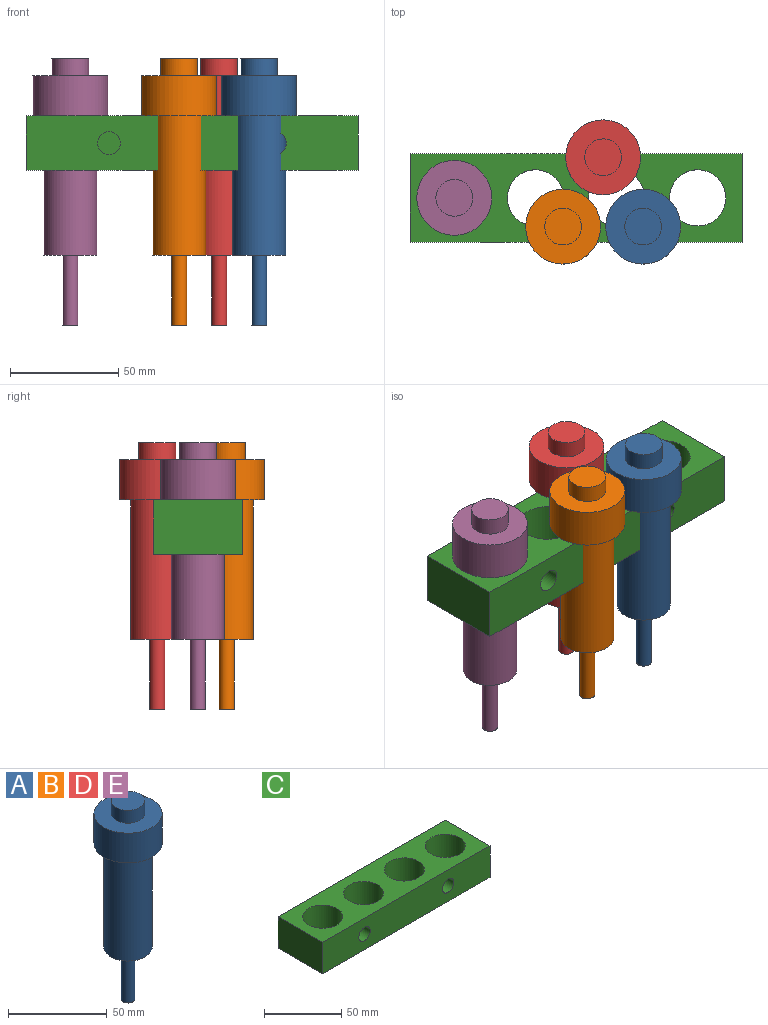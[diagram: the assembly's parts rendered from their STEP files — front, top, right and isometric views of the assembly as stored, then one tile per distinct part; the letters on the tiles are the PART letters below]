
ASSEMBLY  parts=5 mates=1
PART A: 9 faces, bbox 34.6x34.6x123.3 mm
  f0: plane 34.6x34.6mm, normal (0,0,1), area 713.3mm2, adj f1,f7
  f1: cylinder r=17.3mm len=34.6mm, axis (0,0,1), area 2010.9mm2, adj f0,f2
  f2: plane 34.6x34.6mm, normal (0,0,-1), area 465mm2, adj f1,f3
  f3: cylinder r=12.3mm len=64.5mm, axis (0,0,1), area 4984.8mm2, adj f2,f4
  f4: plane 24.6x24.6mm, normal (0,0,-1), area 436.8mm2, adj f3,f5
  f5: cylinder r=3.5mm len=32.3mm, axis (0,0,1), area 710.3mm2, adj f4,f6
  f6: plane 7x7mm, normal (0,0,-1), area 38.5mm2, adj f5
  f7: cylinder r=8.5mm len=17mm, axis (0,0,-1), area 427.3mm2, adj f0,f8
  f8: plane 17x17mm, normal (0,0,1), area 227mm2, adj f7
PART B: same geometry as A
PART C: 14 faces, bbox 153.5x41x25 mm
  f0: plane 41x25mm, normal (1,0,0), area 1025mm2, adj f1,f6,f8,f9
  f1: plane 153.5x25mm, normal (0,1,0), area 3837.5mm2, adj f0,f2,f8,f9
  f2: plane 41x25mm, normal (-1,0,0), area 1025mm2, adj f1,f6,f8,f9
  f3: cylinder r=13mm len=26mm, axis (0,0,-1), area 2042mm2, adj f8,f9
  f4: cylinder r=13mm len=26mm, axis (0,0,-1), area 2042mm2, adj f8,f9
  f5: cylinder r=13mm len=26mm, axis (0,0,-1), area 2042mm2, adj f8,f9
  f6: plane 153.5x25mm, normal (0,-1,0), area 3664.3mm2, adj f0,f2,f8,f9,f10,f12
  f7: cylinder r=13mm len=26mm, axis (0,0,-1), area 2042mm2, adj f8,f9
  f8: plane 153.5x41mm, normal (0,0,1), area 4169.8mm2, adj f0,f1,f2,f3,f4,f5,f6,f7
  f9: plane 153.5x41mm, normal (0,0,-1), area 4169.8mm2, adj f0,f1,f2,f3,f4,f5,f6,f7
  f10: cylinder r=5.25mm len=10.5mm, axis (0,-1,0), area 346.4mm2, adj f6,f11
  f11: plane 10.5x10.5mm, normal (0,-1,0), area 86.6mm2, adj f10
  f12: cylinder r=5.25mm len=10.5mm, axis (0,-1,0), area 346.4mm2, adj f6,f13
  f13: plane 10.5x10.5mm, normal (0,-1,0), area 86.6mm2, adj f12
PART D: same geometry as A
PART E: same geometry as A
PLACE A t=(31.03,13.68,-43)mm
PLACE B t=(-5.97,13.68,-43)mm
PLACE C at identity
PLACE D t=(12.53,45.73,-43)mm
PLACE E t=(-56.25,27,-43)mm
MATE fastened E.f1 <-> C.f5  axis (0,0,1) through (-56.25,0,25)mm
